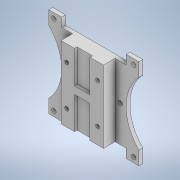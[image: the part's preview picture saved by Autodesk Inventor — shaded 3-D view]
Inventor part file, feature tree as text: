
AUTODESK INVENTOR PART (.ipt)
format: ipt  version: 2022.2 (Build 262287010, 287A)  size: 252,928 bytes
history: native  units: mm
features: extrude x5, sketch x5
ambient origin geometry x8: Origin, YZ Plane, XZ Plane, XY Plane, X Axis, Y Axis, Z Axis, Center Point
bodies: Solid1 (feature_tree)
feature tree (10):
  extrude  "Extrusion1"  Depth=70.0mm
  extrude  "Extrusão4"  Depth=70.0mm
  extrude  "Extrusão5"  Depth=25.0mm
  extrude  "Extrusão6"  Depth=35.0mm
  extrude  "Extrusão7"  Depth=25.0mm
  sketch  "Esboço7"  dims[d15=12.0mm d16=25.0mm d17=7.0mm d18=35.0mm d21=3.0mm d22=12.5mm d24=9.0mm d25=6.0mm d26=3.0mm d27=9.0mm d28=6.0mm d29=12.5mm d30=9.0mm d31=6.0mm d32=3.0mm d33=12.5mm d34=3.0mm d35=9.0mm d36=12.5mm d37=6.0mm d38=9.0mm d39=0.0mm d40=56.0mm d41=16.5mm d42=16.5mm d43=70.0mm d44=12.0mm d45=25.0mm d46=7.0mm d47=35.0mm d48=12.0mm d49=25.0mm d50=7.0mm d51=35.0mm d52=3.0mm d53=12.5mm d54=9.0mm d55=6.0mm d56=3.0mm d57=9.0mm d58=6.0mm d59=12.5mm d60=9.0mm d61=6.0mm d62=3.0mm d63=12.5mm d64=3.0mm d65=9.0mm d66=12.5mm d67=6.0mm d68=56.0mm d69=16.5mm d70=16.5mm d71=2.0mm d72=0.0mm d73=50.0mm d74=25.0mm d75=7.0mm d76=50.0mm d77=7.0mm d78=25.0mm d79=2.0mm d80=0.0mm d81=70.0mm d82=25.0mm d83=35.0mm d84=70.0mm d85=25.0mm d86=35.0mm d87=10.0mm d88=0.0mm d89=3.5mm d90=3.5mm d91=3.5mm d92=3.5mm d93=4.0mm d94=4.0mm d95=4.0mm d96=4.0mm d97=4.0mm d98=4.0mm d99=4.0mm d100=4.0mm d101=3.5mm d102=4.0mm d103=35.0mm d104=3.5mm d105=4.0mm d106=35.0mm]
  sketch  "Sketch1"  dims[d0=70.0mm d1=70.0mm]
  sketch  "Esboço4"  dims[d2=3.0mm d3=0.0mm d10=70.0mm]
  sketch  "Esboço5"  dims[d11=12.0mm d12=25.0mm]
  sketch  "Esboço6"  dims[d13=7.0mm d14=35.0mm]
